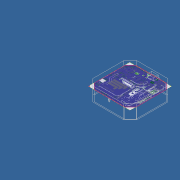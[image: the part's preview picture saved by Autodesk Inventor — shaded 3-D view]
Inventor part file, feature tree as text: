
AUTODESK INVENTOR PART (.ipt)
format: ipt  version: unknown  size: 1,231,872 bytes
history: native  units: mm
features: sketch x10, extrude x9, other x1
ambient origin geometry x8: Origin, YZ Plane, XZ Plane, XY Plane, X Axis, Y Axis, Z Axis, Center Point
bodies: Solido1 (feature_tree)
feature tree (20):
  extrude  "Estrusione1"  Depth=15.0mm TaperAngle=0.0deg
  extrude  "Estrusione6"  Depth=59.0mm
  sketch  "Schizzo8"
  extrude  "Estrusione7"  Depth=59.0mm
  extrude  "Estrusione8"  Depth=8.0mm
  extrude  "Estrusione9"  Depth=8.0mm
  extrude  "Estrusione10"  Depth=59.0mm
  extrude  "Estrusione11"  Depth=8.0mm
  extrude  "Estrusione12"  Depth=8.0mm
  extrude  "Estrusione13"  Depth=8.0mm
  sketch  "Schizzo1"
  sketch  "Schizzo7"
  other  "Immagine2"
  sketch  "Schizzo9"
  sketch  "Schizzo10"
  sketch  "Schizzo11"
  sketch  "Schizzo12"
  sketch  "Schizzo13"
  sketch  "Schizzo14"
  sketch  "Schizzo15"
